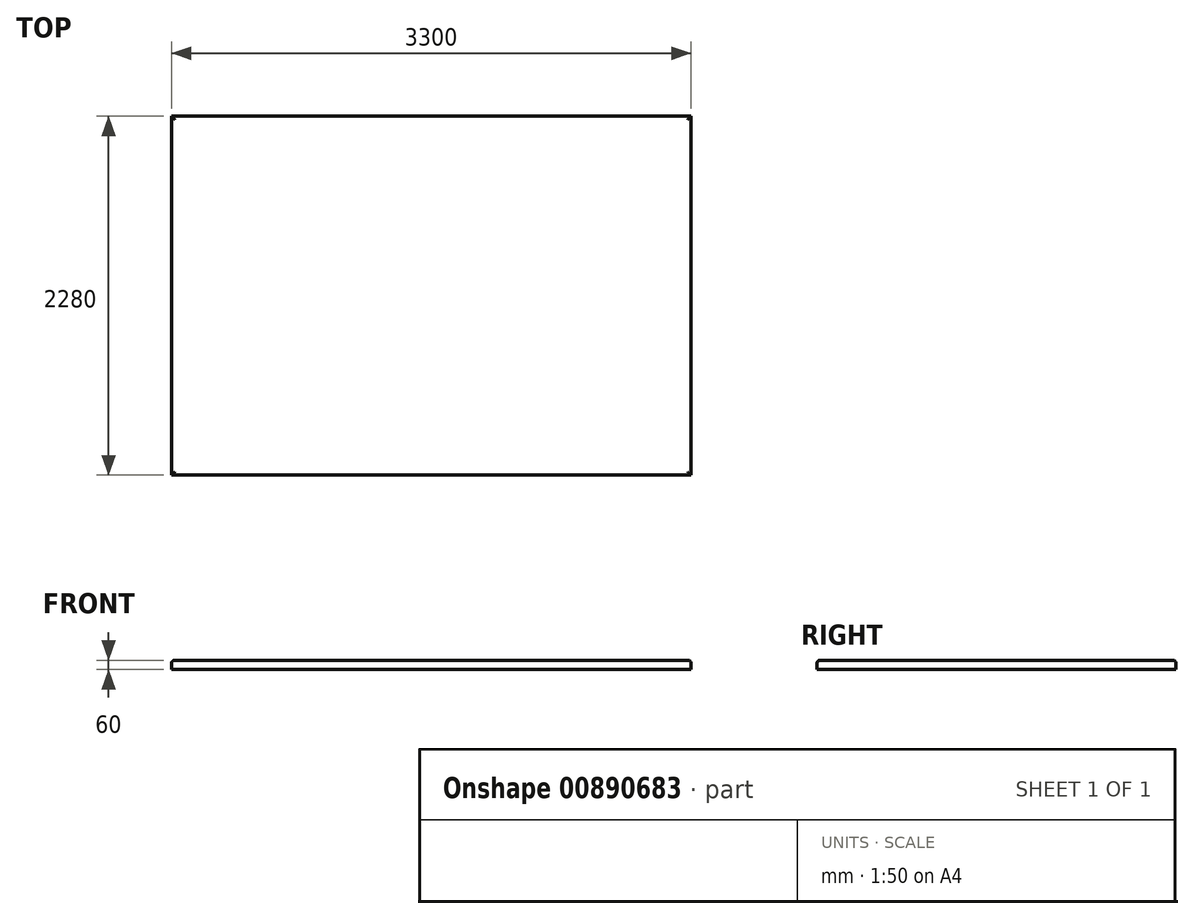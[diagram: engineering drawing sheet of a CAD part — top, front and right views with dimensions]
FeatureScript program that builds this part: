
annotation { "Feature Type Name" : "Feature", "Feature Type Description" : "" }
export const myFeature = defineFeature(function(context is Context, id is Id, definition is map)
    precondition{}
    {
        {
            var Q0;
            Q0=qCreatedBy(makeId("Top.planeOp"),FACE);
            var sketch = newSketch(context, id + "F0", { "sketchPlane" : qUnion([Q0])});
            skLineSegment(sketch, "E0.bottom", {"start": v(2172.14, 1265.48) * mm, "end": v(-1127.86, 1265.48) * mm});
            skLineSegment(sketch, "E0.top", {"start": v(2172.14, -1014.52) * mm, "end": v(-1127.86, -1014.52) * mm});
            skLineSegment(sketch, "E0.left", {"start": v(2172.14, 1265.48) * mm, "end": v(2172.14, -1014.52) * mm});
            skLineSegment(sketch, "E0.right", {"start": v(-1127.86, 1265.48) * mm, "end": v(-1127.86, -1014.52) * mm});
            skSolve(sketch);
        }
        {
            var Q0;
            Q0=makeQuery(id+"F0.imprint","IMPRINT",FACE,{"disambiguationData":[TD([[makeQuery(id+"F0.imprint","IMPRINT",EDGE,{"derivedFrom":sQuery(id+"F0.wireOp",EDGE,"E0.bottom")}),1.0]])]});
            var sketch = newSketch(context, id + "F1", { "sketchPlane" : qUnion([Q0])});
            skSolve(sketch);
        }
        {
            var Q0;
            Q0=makeQuery(id+"F1.imprint","IMPRINT",FACE,{"disambiguationData":[TD([[makeQuery(id+"F1.imprint","IMPRINT",EDGE,{"derivedFrom":makeQuery(id+"F0.imprint","IMPRINT",EDGE,{"derivedFrom":sQuery(id+"F0.wireOp",EDGE,"E0.bottom")})}),1.0]])]});
            extrude(context, id + "F2", {"entities" : qUnion([Q0]), "depth" : 60 * mm, "offsetDistance" : 25 * mm});
        }
        {
            var Q0;
            Q0=makeQuery(id+"F2.opExtrude","CAP_EDGE",EDGE,{"disambiguationData":[OSD([sQuery(id+"F0.wireOp",EDGE,"E0.left")])],"isStart":false});
            var Q1;
            Q1=makeQuery(id+"F2.opExtrude","CAP_EDGE",EDGE,{"disambiguationData":[OSD([sQuery(id+"F0.wireOp",EDGE,"E0.top")])],"isStart":false});
            var Q2;
            Q2=makeQuery(id+"F2.opExtrude","CAP_EDGE",EDGE,{"disambiguationData":[OSD([sQuery(id+"F0.wireOp",EDGE,"E0.right")])],"isStart":false});
            var Q3;
            Q3=makeQuery(id+"F2.opExtrude","CAP_EDGE",EDGE,{"disambiguationData":[OSD([sQuery(id+"F0.wireOp",EDGE,"E0.bottom")])],"isStart":false});
            fillet(context, id + "F3", {"entities" : qUnion([Q0, Q1, Q2, Q3]), "radius" : 20 * mm, "tangentPropagation" : true, "allowEdgeOverflow" : false});
        }
    });
